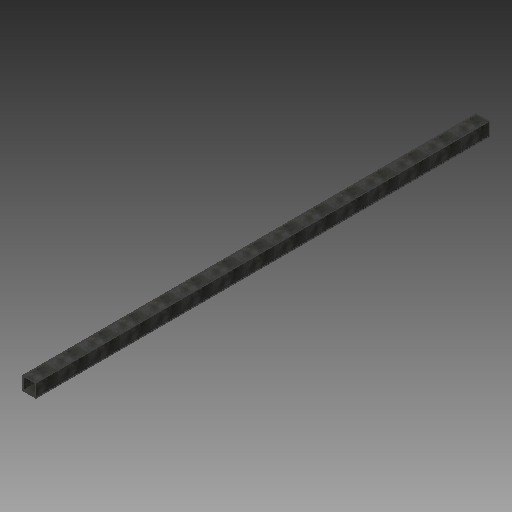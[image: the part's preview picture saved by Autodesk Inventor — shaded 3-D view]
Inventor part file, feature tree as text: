
AUTODESK INVENTOR PART (.ipt)
format: ipt  version: 2018 (Build 220112000, 112)  size: 104,960 bytes
history: native  units: mm
features: other x1, extrude x1, sketch x1
ambient origin geometry x8: Origin, YZ Plane, XZ Plane, XY Plane, X Axis, Y Axis, Z Axis, Center Point
bodies: Body1 (feature_tree)
feature tree (3):
  other  "Sólido1"
  extrude  "Extrusión1"  Depth=75.0mm
  sketch  "Boceto1"  dims[d0=75.0mm d1=75.0mm d2=3.0mm d3=37.5mm d4=37.5mm d5=2570.0mm d6=0.0mm]
